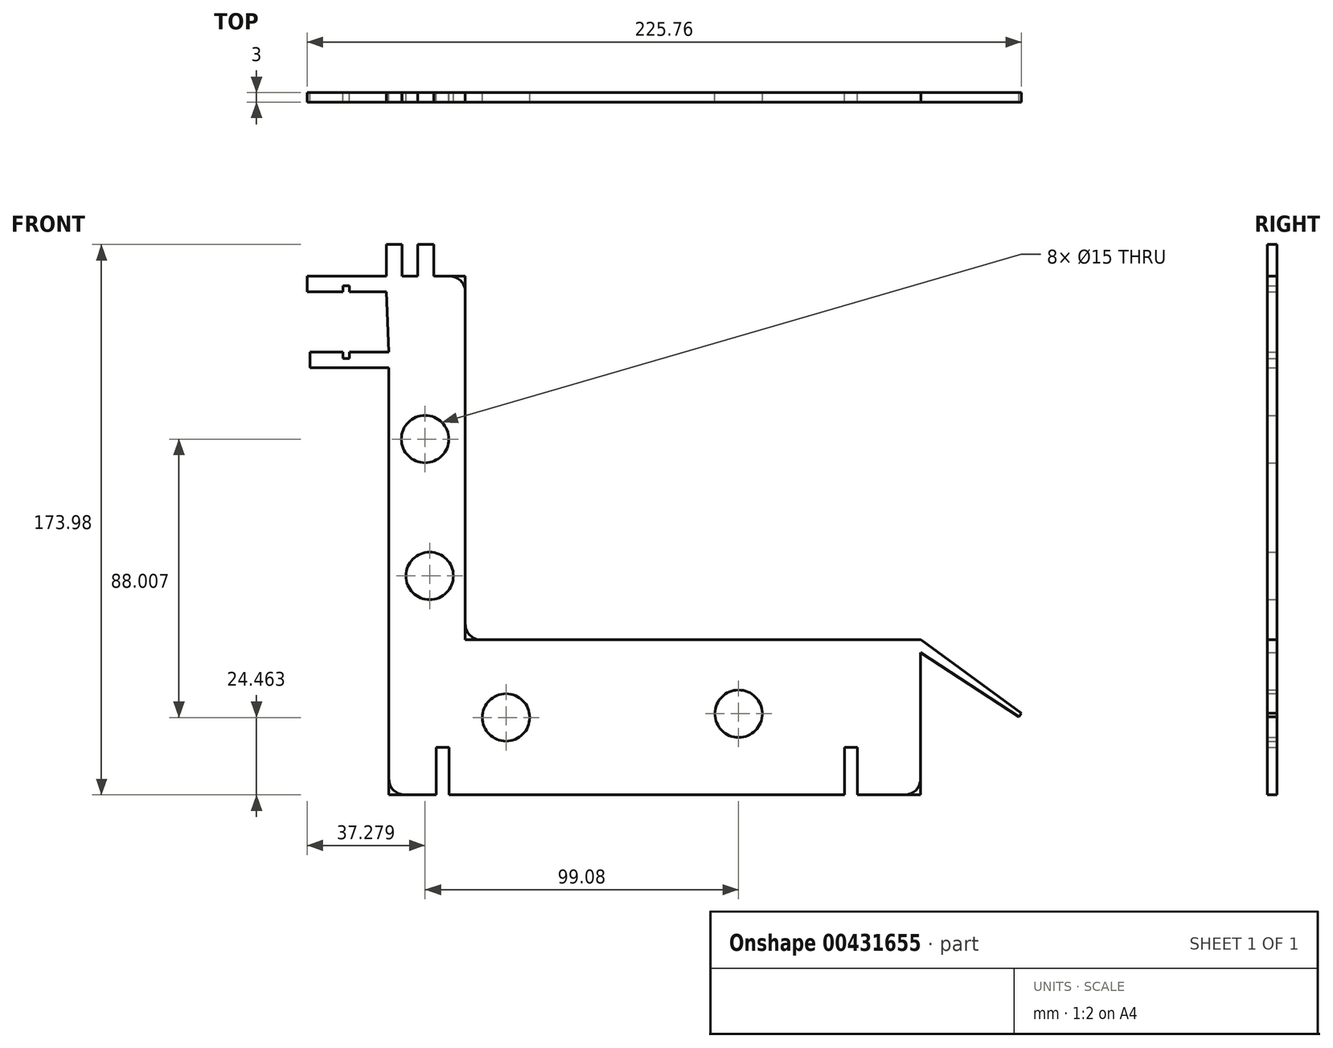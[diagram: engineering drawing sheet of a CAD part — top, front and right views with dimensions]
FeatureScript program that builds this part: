
annotation { "Feature Type Name" : "Feature", "Feature Type Description" : "" }
export const myFeature = defineFeature(function(context is Context, id is Id, definition is map)
    precondition{}
    {
        {
            var Q0;
            Q0=qCreatedBy(makeId("Front.planeOp"),FACE);
            var sketch = newSketch(context, id + "F0", { "sketchPlane" : qUnion([Q0])});
            skLineSegment(sketch, "E0", {"start": v(-70.7, 51.51) * mm, "end": v(-45.7, 51.51) * mm});
            skLineSegment(sketch, "E1", {"start": v(-45.7, 51.51) * mm, "end": v(-45.7, 61.51) * mm});
            skLineSegment(sketch, "E2", {"start": v(-45.7, 61.51) * mm, "end": v(-40.7, 61.51) * mm});
            skLineSegment(sketch, "E3", {"start": v(-40.7, 61.51) * mm, "end": v(-40.7, 51.51) * mm});
            skLineSegment(sketch, "E4", {"start": v(-40.7, 51.51) * mm, "end": v(-35.7, 51.51) * mm});
            skLineSegment(sketch, "E5", {"start": v(-35.7, 51.51) * mm, "end": v(-35.7, 61.51) * mm});
            skLineSegment(sketch, "E6", {"start": v(-35.7, 61.51) * mm, "end": v(-30.7, 61.51) * mm});
            skLineSegment(sketch, "E7", {"start": v(-30.7, 61.51) * mm, "end": v(-30.7, 51.51) * mm});
            skLineSegment(sketch, "E8", {"start": v(-70.7, 51.51) * mm, "end": v(-70.7, 46.51) * mm});
            skLineSegment(sketch, "E9", {"start": v(-70.7, 46.51) * mm, "end": v(-59.35, 46.51) * mm});
            skLineSegment(sketch, "E10", {"start": v(-63.62, 46.51) * mm, "end": v(-59.35, 46.51) * mm});
            skPoint(sketch, "E11.start.orphan", {"position": v(-69.85, 27.53) * mm});
            skLineSegment(sketch, "E12", {"start": v(-69.85, 27.53) * mm, "end": v(-59.35, 27.53) * mm});
            skLineSegment(sketch, "E13", {"start": v(-69.85, 27.53) * mm, "end": v(-69.85, 22.53) * mm});
            skLineSegment(sketch, "E14", {"start": v(-69.85, 22.53) * mm, "end": v(-44.85, 22.53) * mm});
            skLineSegment(sketch, "E15", {"start": v(-44.85, 22.53) * mm, "end": v(-44.85, -112.47) * mm});
            skLineSegment(sketch, "E16", {"start": v(-44.85, -112.47) * mm, "end": v(-29.85, -112.47) * mm});
            skLineSegment(sketch, "E17", {"start": v(-29.85, -112.47) * mm, "end": v(-29.85, -97.47) * mm});
            skLineSegment(sketch, "E18", {"start": v(-29.85, -97.47) * mm, "end": v(-25.85, -97.47) * mm});
            skLineSegment(sketch, "E19", {"start": v(-25.85, -97.47) * mm, "end": v(-25.85, -112.47) * mm});
            skLineSegment(sketch, "E20", {"start": v(-25.85, -112.47) * mm, "end": v(99.15, -112.47) * mm});
            skLineSegment(sketch, "E21", {"start": v(99.15, -112.47) * mm, "end": v(99.15, -97.47) * mm});
            skLineSegment(sketch, "E22", {"start": v(99.15, -97.47) * mm, "end": v(103.15, -97.47) * mm});
            skLineSegment(sketch, "E23", {"start": v(103.15, -97.47) * mm, "end": v(103.15, -112.47) * mm});
            skLineSegment(sketch, "E24", {"start": v(103.15, -112.47) * mm, "end": v(123.15, -112.47) * mm});
            skLineSegment(sketch, "E25", {"start": v(-45.7, 46.51) * mm, "end": v(-44.85, 27.53) * mm});
            skPoint(sketch, "E26.start.orphan", {"position": v(-70.9, 27.53) * mm});
            skPoint(sketch, "E27.end.orphan", {"position": v(0, 51.51) * mm});
            skLineSegment(sketch, "E28", {"start": v(123.15, -112.47) * mm, "end": v(123.15, -67.47) * mm});
            skLineSegment(sketch, "E29", {"start": v(-30.7, 51.51) * mm, "end": v(-20.7, 51.51) * mm});
            skLineSegment(sketch, "E30", {"start": v(-20.7, 51.51) * mm, "end": v(-20.7, -63.49) * mm});
            skLineSegment(sketch, "E31", {"start": v(-20.7, -63.49) * mm, "end": v(123.3, -63.49) * mm});
            skPoint(sketch, "E32.orphan", {"position": v(123.3, -69.22) * mm});
            skLineSegment(sketch, "E33", {"start": v(123.15, -67.47) * mm, "end": v(154.29, -87.8) * mm});
            skLineSegment(sketch, "E34", {"start": v(154.29, -87.8) * mm, "end": v(155.06, -86.63) * mm});
            skLineSegment(sketch, "E35", {"start": v(155.06, -86.63) * mm, "end": v(123.3, -63.49) * mm});
            skLineSegment(sketch, "E36", {"start": v(-57.35, 27.53) * mm, "end": v(-57.35, 25.53) * mm});
            skPoint(sketch, "E36.endSnap0", {"position": v(-57.35, 22.53) * mm});
            skLineSegment(sketch, "E37", {"start": v(-57.35, 25.53) * mm, "end": v(-59.35, 25.53) * mm});
            skLineSegment(sketch, "E38", {"start": v(-59.35, 25.53) * mm, "end": v(-59.35, 27.53) * mm});
            skLineSegment(sketch, "E39.trimOffspring", {"start": v(-57.35, 27.53) * mm, "end": v(-44.85, 27.53) * mm});
            skLineSegment(sketch, "E40", {"start": v(-59.35, 46.51) * mm, "end": v(-59.35, 48.51) * mm});
            skLineSegment(sketch, "E41", {"start": v(-59.35, 48.51) * mm, "end": v(-57.35, 48.51) * mm});
            skLineSegment(sketch, "E42", {"start": v(-57.35, 48.51) * mm, "end": v(-57.35, 46.51) * mm});
            skPoint(sketch, "E43.orphan", {"position": v(-58.2, 46.51) * mm});
            skLineSegment(sketch, "E44.trimOffspring", {"start": v(-57.35, 46.51) * mm, "end": v(-45.7, 46.51) * mm});
            skCircle(sketch, "E45", {"center": v(-33.42, 0) * mm, "radius": 7.5 * mm});
            skCircle(sketch, "E46", {"center": v(-31.97, -43.26) * mm, "radius": 7.5 * mm});
            skCircle(sketch, "E47", {"center": v(65.66, -86.84) * mm, "radius": 7.5 * mm});
            skCircle(sketch, "E48", {"center": v(-7.85, -88) * mm, "radius": 7.5 * mm});
            skSolve(sketch);
        }
        {
            var Q0;
            Q0=makeQuery(id+"F0.imprint","IMPRINT",FACE,{"disambiguationData":[TD([[makeQuery(id+"F0.imprint","IMPRINT",EDGE,{"derivedFrom":sQuery(id+"F0.wireOp",EDGE,"E0")}),-1.0]])]});
            extrude(context, id + "F1", {"entities" : qUnion([Q0]), "depth" : 3 * mm});
        }
        {
            var Q0;
            Q0=makeQuery(id+"F1.opExtrude","SWEPT_EDGE",EDGE,{"disambiguationData":[OSD([sQuery(id+"F0.wireOp",EDGE,"E29"),sQuery(id+"F0.wireOp",EDGE,"E30")])]});
            fillet(context, id + "F2", {"entities" : qUnion([Q0]), "radius" : 5 * mm, "tangentPropagation" : true, "allowEdgeOverflow" : false});
        }
        {
            var Q0;
            Q0=makeQuery(id+"F1.opExtrude","SWEPT_EDGE",EDGE,{"disambiguationData":[OSD([sQuery(id+"F0.wireOp",EDGE,"E24"),sQuery(id+"F0.wireOp",EDGE,"E28")])]});
            fillet(context, id + "F3", {"entities" : qUnion([Q0]), "radius" : 5 * mm, "tangentPropagation" : true, "allowEdgeOverflow" : false});
        }
        {
            var Q0;
            Q0=makeQuery(id+"F1.opExtrude","SWEPT_EDGE",EDGE,{"disambiguationData":[OSD([sQuery(id+"F0.wireOp",EDGE,"E15"),sQuery(id+"F0.wireOp",EDGE,"E16")])]});
            fillet(context, id + "F4", {"entities" : qUnion([Q0]), "radius" : 5 * mm, "tangentPropagation" : true, "allowEdgeOverflow" : false});
        }
        {
            var Q0;
            Q0=makeQuery(id+"F1.opExtrude","SWEPT_EDGE",EDGE,{"disambiguationData":[OSD([sQuery(id+"F0.wireOp",EDGE,"E30"),sQuery(id+"F0.wireOp",EDGE,"E31")])]});
            fillet(context, id + "F5", {"entities" : qUnion([Q0]), "radius" : 5 * mm, "tangentPropagation" : true, "allowEdgeOverflow" : false});
        }
        {
            var Q0;
            Q0=makeQuery(id+"F0.imprint","IMPRINT",FACE,{"disambiguationData":[TD([[makeQuery(id+"F0.imprint","IMPRINT",EDGE,{"derivedFrom":sQuery(id+"F0.wireOp",EDGE,"E0")}),-1.0]])]});
            extrude(context, id + "F6", {"entities" : qUnion([Q0]), "depth" : 3 * mm});
        }
    });
